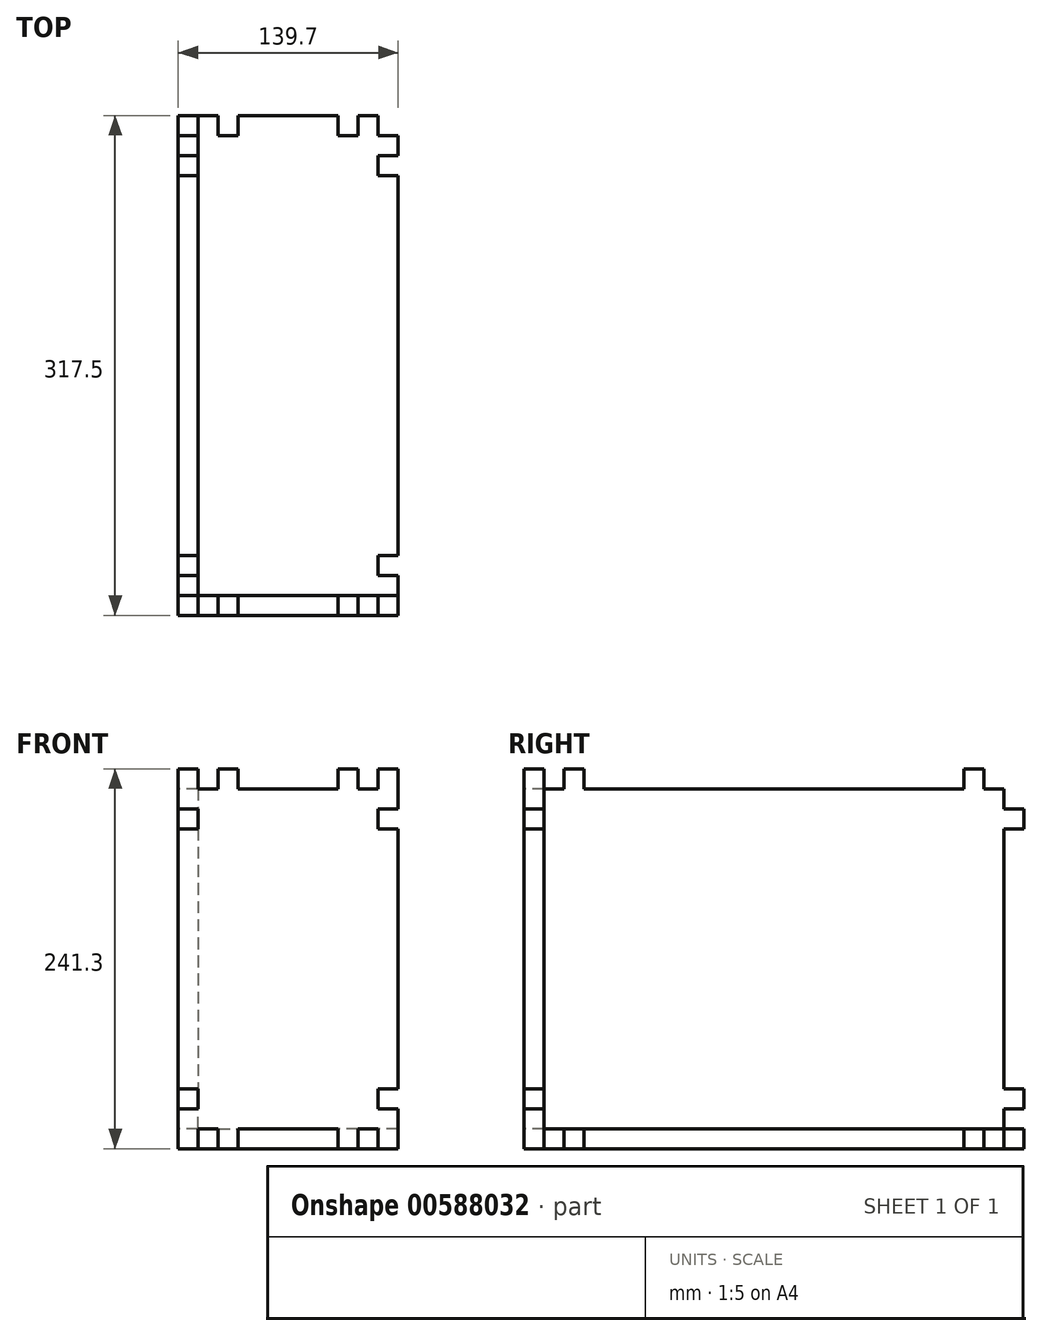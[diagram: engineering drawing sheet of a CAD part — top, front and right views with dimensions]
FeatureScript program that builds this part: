
annotation { "Feature Type Name" : "Feature", "Feature Type Description" : "" }
export const myFeature = defineFeature(function(context is Context, id is Id, definition is map)
    precondition{}
    {
        {
            var Q0;
            Q0=qCreatedBy(makeId("Top.planeOp"),FACE);
            var sketch = newSketch(context, id + "F0", { "sketchPlane" : qUnion([Q0])});
            skLineSegment(sketch, "E0.bottom", {"start": v(0, 0) * mm, "end": v(139.7, 0) * mm});
            skLineSegment(sketch, "E0.top", {"start": v(0, 317.5) * mm, "end": v(139.7, 317.5) * mm});
            skLineSegment(sketch, "E0.left", {"start": v(0, 0) * mm, "end": v(0, 317.5) * mm});
            skLineSegment(sketch, "E0.right", {"start": v(139.7, 0) * mm, "end": v(139.7, 317.5) * mm});
            skLineSegment(sketch, "E1", {"start": v(0, 0) * mm, "end": v(0, 12.7) * mm});
            skLineSegment(sketch, "E2", {"start": v(0, 12.7) * mm, "end": v(12.7, 12.7) * mm});
            skLineSegment(sketch, "E3", {"start": v(12.7, 12.7) * mm, "end": v(12.7, 0) * mm});
            skLineSegment(sketch, "E4", {"start": v(12.7, 0) * mm, "end": v(25.4, 0) * mm});
            skLineSegment(sketch, "E5", {"start": v(25.4, 0) * mm, "end": v(25.4, 12.7) * mm});
            skLineSegment(sketch, "E6", {"start": v(25.4, 12.7) * mm, "end": v(38.1, 12.7) * mm});
            skLineSegment(sketch, "E7", {"start": v(38.1, 12.7) * mm, "end": v(38.1, 0) * mm});
            skLineSegment(sketch, "E8", {"start": v(0, 12.7) * mm, "end": v(0, 25.4) * mm});
            skLineSegment(sketch, "E9", {"start": v(0, 25.4) * mm, "end": v(12.7, 25.4) * mm});
            skLineSegment(sketch, "E10", {"start": v(12.7, 25.4) * mm, "end": v(12.7, 38.1) * mm});
            skLineSegment(sketch, "E11", {"start": v(12.7, 38.1) * mm, "end": v(0, 38.1) * mm});
            skLineSegment(sketch, "E12", {"start": v(0, 158.75) * mm, "end": v(30.82, 158.75) * mm});
            skLineSegment(sketch, "E13", {"start": v(69.85, 0) * mm, "end": v(69.85, 38.66) * mm});
            skLineSegment(sketch, "E14.MirrorCS", {"start": v(0, 292.1) * mm, "end": v(12.7, 292.1) * mm});
            skLineSegment(sketch, "E15.MirrorCS", {"start": v(0, 304.8) * mm, "end": v(0, 292.1) * mm});
            skLineSegment(sketch, "E16.MirrorCS", {"start": v(12.7, 292.1) * mm, "end": v(12.7, 279.4) * mm});
            skLineSegment(sketch, "E17.MirrorCS", {"start": v(12.7, 279.4) * mm, "end": v(0, 279.4) * mm});
            skLineSegment(sketch, "E18.MirrorCS", {"start": v(0, 317.5) * mm, "end": v(0, 304.8) * mm});
            skLineSegment(sketch, "E19.MirrorCS", {"start": v(38.1, 304.8) * mm, "end": v(38.1, 317.5) * mm});
            skLineSegment(sketch, "E20.MirrorCS", {"start": v(25.4, 304.8) * mm, "end": v(38.1, 304.8) * mm});
            skLineSegment(sketch, "E21.MirrorCS", {"start": v(25.4, 317.5) * mm, "end": v(25.4, 304.8) * mm});
            skLineSegment(sketch, "E22.MirrorCS", {"start": v(12.7, 317.5) * mm, "end": v(25.4, 317.5) * mm});
            skLineSegment(sketch, "E23.MirrorCS", {"start": v(0, 304.8) * mm, "end": v(12.7, 304.8) * mm});
            skLineSegment(sketch, "E24.MirrorCS", {"start": v(12.7, 304.8) * mm, "end": v(12.7, 317.5) * mm});
            skLineSegment(sketch, "E25.MirrorCS", {"start": v(0, 317.5) * mm, "end": v(0, 0) * mm});
            skLineSegment(sketch, "E26.MirrorCS", {"start": v(101.6, 304.8) * mm, "end": v(101.6, 317.5) * mm});
            skLineSegment(sketch, "E27.MirrorCS", {"start": v(114.3, 304.8) * mm, "end": v(101.6, 304.8) * mm});
            skLineSegment(sketch, "E28.MirrorCS", {"start": v(127, 317.5) * mm, "end": v(114.3, 317.5) * mm});
            skLineSegment(sketch, "E29.MirrorCS", {"start": v(114.3, 317.5) * mm, "end": v(114.3, 304.8) * mm});
            skLineSegment(sketch, "E30.MirrorCS", {"start": v(127, 304.8) * mm, "end": v(127, 317.5) * mm});
            skLineSegment(sketch, "E31.MirrorCS", {"start": v(139.7, 304.8) * mm, "end": v(127, 304.8) * mm});
            skLineSegment(sketch, "E32.MirrorCS", {"start": v(139.7, 304.8) * mm, "end": v(139.7, 292.1) * mm});
            skLineSegment(sketch, "E33.MirrorCS", {"start": v(139.7, 292.1) * mm, "end": v(127, 292.1) * mm});
            skLineSegment(sketch, "E34.MirrorCS", {"start": v(127, 292.1) * mm, "end": v(127, 279.4) * mm});
            skLineSegment(sketch, "E35.MirrorCS", {"start": v(127, 279.4) * mm, "end": v(139.7, 279.4) * mm});
            skLineSegment(sketch, "E36.MirrorCS", {"start": v(127, 38.1) * mm, "end": v(139.7, 38.1) * mm});
            skLineSegment(sketch, "E37.MirrorCS", {"start": v(101.6, 12.7) * mm, "end": v(101.6, 0) * mm});
            skLineSegment(sketch, "E38.MirrorCS", {"start": v(114.3, 12.7) * mm, "end": v(101.6, 12.7) * mm});
            skLineSegment(sketch, "E39.MirrorCS", {"start": v(127, 0) * mm, "end": v(114.3, 0) * mm});
            skLineSegment(sketch, "E40.MirrorCS", {"start": v(114.3, 0) * mm, "end": v(114.3, 12.7) * mm});
            skLineSegment(sketch, "E41.MirrorCS", {"start": v(127, 12.7) * mm, "end": v(127, 0) * mm});
            skLineSegment(sketch, "E42.MirrorCS", {"start": v(139.7, 12.7) * mm, "end": v(127, 12.7) * mm});
            skLineSegment(sketch, "E43.MirrorCS", {"start": v(139.7, 12.7) * mm, "end": v(139.7, 25.4) * mm});
            skLineSegment(sketch, "E44.MirrorCS", {"start": v(127, 25.4) * mm, "end": v(127, 38.1) * mm});
            skLineSegment(sketch, "E45.MirrorCS", {"start": v(139.7, 25.4) * mm, "end": v(127, 25.4) * mm});
            skSolve(sketch);
        }
        {
            var Q0;
            Q0=makeQuery(id+"F0.imprint","IMPRINT",FACE,{"disambiguationData":[TD([[makeQuery(id+"F0.imprint","IMPRINT",EDGE,{"derivedFrom":sQuery(id+"F0.wireOp",EDGE,"E16.MirrorCS")}),1.0]])]});
            extrude(context, id + "F1", {"entities" : qUnion([Q0]), "oppositeDirection" : true, "depth" : 12.7 * mm, "offsetDistance" : 25.4 * mm});
        }
        {
            var Q0;
            Q0=qCreatedBy(makeId("Front.planeOp"),FACE);
            var sketch = newSketch(context, id + "F2", { "sketchPlane" : qUnion([Q0])});
            skLineSegment(sketch, "E46", {"start": v(0, 0) * mm, "end": v(0, -12.7) * mm});
            skLineSegment(sketch, "E47", {"start": v(0, -12.7) * mm, "end": v(12.7, -12.7) * mm});
            skLineSegment(sketch, "E48", {"start": v(12.7, -12.7) * mm, "end": v(12.7, 0) * mm});
            skLineSegment(sketch, "E49", {"start": v(12.7, 0) * mm, "end": v(25.4, 0) * mm});
            skLineSegment(sketch, "E50", {"start": v(25.4, 0) * mm, "end": v(25.4, -12.7) * mm});
            skLineSegment(sketch, "E51", {"start": v(25.4, -12.7) * mm, "end": v(38.1, -12.7) * mm});
            skLineSegment(sketch, "E52", {"start": v(0, 0) * mm, "end": v(0, 12.7) * mm});
            skLineSegment(sketch, "E53", {"start": v(0, 12.7) * mm, "end": v(12.7, 12.7) * mm});
            skLineSegment(sketch, "E54", {"start": v(12.7, 12.7) * mm, "end": v(12.7, 25.4) * mm});
            skLineSegment(sketch, "E55", {"start": v(12.7, 25.4) * mm, "end": v(0, 25.4) * mm});
            skLineSegment(sketch, "E56.bottom", {"start": v(0, -12.7) * mm, "end": v(139.7, -12.7) * mm});
            skLineSegment(sketch, "E56.top", {"start": v(0, 228.6) * mm, "end": v(139.7, 228.6) * mm});
            skLineSegment(sketch, "E56.left", {"start": v(0, -12.7) * mm, "end": v(0, 228.6) * mm});
            skLineSegment(sketch, "E56.right", {"start": v(139.7, -12.7) * mm, "end": v(139.7, 228.6) * mm});
            skLineSegment(sketch, "E57", {"start": v(69.85, -12.7) * mm, "end": v(69.85, 21.02) * mm});
            skLineSegment(sketch, "E58", {"start": v(0, 107.95) * mm, "end": v(42.02, 107.95) * mm});
            skLineSegment(sketch, "E59.MirrorCS", {"start": v(127, -12.7) * mm, "end": v(127, 0) * mm});
            skLineSegment(sketch, "E60.MirrorCS", {"start": v(114.3, -12.7) * mm, "end": v(101.6, -12.7) * mm});
            skLineSegment(sketch, "E61.MirrorCS", {"start": v(127, 0) * mm, "end": v(114.3, 0) * mm});
            skLineSegment(sketch, "E62.MirrorCS", {"start": v(139.7, 0) * mm, "end": v(139.7, 12.7) * mm});
            skLineSegment(sketch, "E63.MirrorCS", {"start": v(127, 12.7) * mm, "end": v(127, 25.4) * mm});
            skLineSegment(sketch, "E64.MirrorCS", {"start": v(139.7, 12.7) * mm, "end": v(127, 12.7) * mm});
            skLineSegment(sketch, "E65.MirrorCS", {"start": v(139.7, -12.7) * mm, "end": v(127, -12.7) * mm});
            skLineSegment(sketch, "E66.MirrorCS", {"start": v(139.7, 0) * mm, "end": v(139.7, -12.7) * mm});
            skLineSegment(sketch, "E67.MirrorCS", {"start": v(114.3, 0) * mm, "end": v(114.3, -12.7) * mm});
            skLineSegment(sketch, "E68.MirrorCS", {"start": v(127, 25.4) * mm, "end": v(139.7, 25.4) * mm});
            skLineSegment(sketch, "E69.MirrorCS", {"start": v(12.7, 190.5) * mm, "end": v(0, 190.5) * mm});
            skLineSegment(sketch, "E70.MirrorCS", {"start": v(12.7, 203.2) * mm, "end": v(12.7, 190.5) * mm});
            skLineSegment(sketch, "E71.MirrorCS", {"start": v(0, 203.2) * mm, "end": v(12.7, 203.2) * mm});
            skLineSegment(sketch, "E72.MirrorCS", {"start": v(0, 228.6) * mm, "end": v(12.7, 228.6) * mm});
            skLineSegment(sketch, "E73.MirrorCS", {"start": v(25.4, 215.9) * mm, "end": v(25.4, 228.6) * mm});
            skLineSegment(sketch, "E74.MirrorCS", {"start": v(12.7, 228.6) * mm, "end": v(12.7, 215.9) * mm});
            skLineSegment(sketch, "E75.MirrorCS", {"start": v(0, 215.9) * mm, "end": v(0, 228.6) * mm});
            skLineSegment(sketch, "E76.MirrorCS", {"start": v(12.7, 215.9) * mm, "end": v(25.4, 215.9) * mm});
            skLineSegment(sketch, "E77.MirrorCS", {"start": v(0, 215.9) * mm, "end": v(0, 203.2) * mm});
            skLineSegment(sketch, "E78.MirrorCS", {"start": v(25.4, 228.6) * mm, "end": v(38.1, 228.6) * mm});
            skLineSegment(sketch, "E79.MirrorCS", {"start": v(139.7, 215.9) * mm, "end": v(139.7, 228.6) * mm});
            skLineSegment(sketch, "E80.MirrorCS", {"start": v(114.3, 228.6) * mm, "end": v(101.6, 228.6) * mm});
            skLineSegment(sketch, "E81.MirrorCS", {"start": v(127, 215.9) * mm, "end": v(114.3, 215.9) * mm});
            skLineSegment(sketch, "E82.MirrorCS", {"start": v(139.7, 228.6) * mm, "end": v(127, 228.6) * mm});
            skLineSegment(sketch, "E83.MirrorCS", {"start": v(127, 228.6) * mm, "end": v(127, 215.9) * mm});
            skLineSegment(sketch, "E84.MirrorCS", {"start": v(139.7, 215.9) * mm, "end": v(139.7, 203.2) * mm});
            skLineSegment(sketch, "E85.MirrorCS", {"start": v(127, 203.2) * mm, "end": v(127, 190.5) * mm});
            skLineSegment(sketch, "E86.MirrorCS", {"start": v(139.7, 228.6) * mm, "end": v(139.7, -12.7) * mm});
            skLineSegment(sketch, "E87.MirrorCS", {"start": v(114.3, 215.9) * mm, "end": v(114.3, 228.6) * mm});
            skLineSegment(sketch, "E88.MirrorCS", {"start": v(127, 190.5) * mm, "end": v(139.7, 190.5) * mm});
            skLineSegment(sketch, "E89.MirrorCS", {"start": v(139.7, 203.2) * mm, "end": v(127, 203.2) * mm});
            skLineSegment(sketch, "E90", {"start": v(38.1, -12.7) * mm, "end": v(38.1, 0) * mm});
            skLineSegment(sketch, "E91", {"start": v(101.6, -12.7) * mm, "end": v(101.6, 0) * mm});
            skLineSegment(sketch, "E92", {"start": v(101.6, 0) * mm, "end": v(38.1, 0) * mm});
            skLineSegment(sketch, "E93", {"start": v(38.1, 228.6) * mm, "end": v(38.1, 215.9) * mm});
            skLineSegment(sketch, "E94", {"start": v(38.1, 215.9) * mm, "end": v(101.6, 215.9) * mm});
            skLineSegment(sketch, "E95", {"start": v(101.6, 215.9) * mm, "end": v(101.6, 228.6) * mm});
            skSolve(sketch);
        }
        {
            var Q0;
            {var subQ10=sQuery(id+"F2.wireOp",EDGE,"E48");Q0=makeQuery(id+"F2.imprint","IMPRINT",FACE,{"disambiguationData":[TD([[makeQuery(id+"F2.imprint","IMPRINT",EDGE,{"derivedFrom":subQ10}),1.0]])]});}
            extrude(context, id + "F3", {"entities" : qUnion([Q0]), "oppositeDirection" : true, "depth" : 12.7 * mm, "offsetDistance" : 25.4 * mm});
        }
        {
            var Q0;
            Q0=qCreatedBy(makeId("Right.planeOp"),FACE);
            var sketch = newSketch(context, id + "F4", { "sketchPlane" : qUnion([Q0])});
            skLineSegment(sketch, "E96", {"start": v(0, 0) * mm, "end": v(12.7, 0) * mm});
            skLineSegment(sketch, "E97", {"start": v(12.7, 0) * mm, "end": v(12.7, 12.7) * mm});
            skLineSegment(sketch, "E98", {"start": v(12.7, 12.7) * mm, "end": v(0, 12.7) * mm});
            skLineSegment(sketch, "E99", {"start": v(0, 12.7) * mm, "end": v(0, 25.4) * mm});
            skLineSegment(sketch, "E100", {"start": v(0, 25.4) * mm, "end": v(12.7, 25.4) * mm});
            skLineSegment(sketch, "E101", {"start": v(12.7, 0) * mm, "end": v(25.4, 0) * mm});
            skLineSegment(sketch, "E102", {"start": v(25.4, 0) * mm, "end": v(25.4, -12.7) * mm});
            skLineSegment(sketch, "E103", {"start": v(25.4, -12.7) * mm, "end": v(38.1, -12.7) * mm});
            skLineSegment(sketch, "E104", {"start": v(38.1, -12.7) * mm, "end": v(38.1, 0) * mm});
            skLineSegment(sketch, "E105", {"start": v(0, 0) * mm, "end": v(0, -12.7) * mm});
            skLineSegment(sketch, "E106.bottom", {"start": v(0, -12.7) * mm, "end": v(317.5, -12.7) * mm});
            skLineSegment(sketch, "E106.top", {"start": v(0, 228.6) * mm, "end": v(317.5, 228.6) * mm});
            skLineSegment(sketch, "E106.left", {"start": v(0, -12.7) * mm, "end": v(0, 228.6) * mm});
            skLineSegment(sketch, "E106.right", {"start": v(317.5, -12.7) * mm, "end": v(317.5, 228.6) * mm});
            skLineSegment(sketch, "E107", {"start": v(158.75, 228.6) * mm, "end": v(158.75, 170.9) * mm});
            skLineSegment(sketch, "E108", {"start": v(0, 107.95) * mm, "end": v(67.23, 107.95) * mm});
            skLineSegment(sketch, "E109.MirrorCS", {"start": v(12.7, 215.9) * mm, "end": v(12.7, 203.2) * mm});
            skLineSegment(sketch, "E110.MirrorCS", {"start": v(0, 215.9) * mm, "end": v(12.7, 215.9) * mm});
            skLineSegment(sketch, "E111.MirrorCS", {"start": v(25.4, 215.9) * mm, "end": v(25.4, 228.6) * mm});
            skLineSegment(sketch, "E112.MirrorCS", {"start": v(38.1, 228.6) * mm, "end": v(38.1, 215.9) * mm});
            skLineSegment(sketch, "E113.MirrorCS", {"start": v(0, 215.9) * mm, "end": v(0, 228.6) * mm});
            skLineSegment(sketch, "E114.MirrorCS", {"start": v(25.4, 228.6) * mm, "end": v(38.1, 228.6) * mm});
            skLineSegment(sketch, "E115.MirrorCS", {"start": v(12.7, 215.9) * mm, "end": v(25.4, 215.9) * mm});
            skLineSegment(sketch, "E116.MirrorCS", {"start": v(0, 190.5) * mm, "end": v(12.7, 190.5) * mm});
            skLineSegment(sketch, "E117.MirrorCS", {"start": v(0, 203.2) * mm, "end": v(0, 190.5) * mm});
            skLineSegment(sketch, "E118.MirrorCS", {"start": v(12.7, 203.2) * mm, "end": v(0, 203.2) * mm});
            skLineSegment(sketch, "E119.MirrorCS", {"start": v(292.1, 0) * mm, "end": v(292.1, -12.7) * mm});
            skLineSegment(sketch, "E120.MirrorCS", {"start": v(304.8, 12.7) * mm, "end": v(317.5, 12.7) * mm});
            skLineSegment(sketch, "E121.MirrorCS", {"start": v(317.5, 12.7) * mm, "end": v(317.5, 25.4) * mm});
            skLineSegment(sketch, "E122.MirrorCS", {"start": v(317.5, 0) * mm, "end": v(304.8, 0) * mm});
            skLineSegment(sketch, "E123.MirrorCS", {"start": v(317.5, 0) * mm, "end": v(317.5, -12.7) * mm});
            skLineSegment(sketch, "E124.MirrorCS", {"start": v(292.1, -12.7) * mm, "end": v(279.4, -12.7) * mm});
            skLineSegment(sketch, "E125.MirrorCS", {"start": v(304.8, 0) * mm, "end": v(292.1, 0) * mm});
            skLineSegment(sketch, "E126.MirrorCS", {"start": v(304.8, 0) * mm, "end": v(304.8, 12.7) * mm});
            skLineSegment(sketch, "E127.MirrorCS", {"start": v(279.4, -12.7) * mm, "end": v(279.4, 0) * mm});
            skLineSegment(sketch, "E128.MirrorCS", {"start": v(317.5, 25.4) * mm, "end": v(304.8, 25.4) * mm});
            skLineSegment(sketch, "E129.MirrorCS", {"start": v(317.5, -12.7) * mm, "end": v(0, -12.7) * mm});
            skLineSegment(sketch, "E130.MirrorCS", {"start": v(317.5, 215.9) * mm, "end": v(304.8, 215.9) * mm});
            skLineSegment(sketch, "E131.MirrorCS", {"start": v(292.1, 228.6) * mm, "end": v(279.4, 228.6) * mm});
            skLineSegment(sketch, "E132.MirrorCS", {"start": v(317.5, 203.2) * mm, "end": v(317.5, 190.5) * mm});
            skLineSegment(sketch, "E133.MirrorCS", {"start": v(292.1, 215.9) * mm, "end": v(292.1, 228.6) * mm});
            skLineSegment(sketch, "E134.MirrorCS", {"start": v(317.5, 215.9) * mm, "end": v(317.5, 228.6) * mm});
            skLineSegment(sketch, "E135.MirrorCS", {"start": v(304.8, 215.9) * mm, "end": v(304.8, 203.2) * mm});
            skLineSegment(sketch, "E136.MirrorCS", {"start": v(304.8, 203.2) * mm, "end": v(317.5, 203.2) * mm});
            skLineSegment(sketch, "E137.MirrorCS", {"start": v(304.8, 215.9) * mm, "end": v(292.1, 215.9) * mm});
            skLineSegment(sketch, "E138.MirrorCS", {"start": v(317.5, 190.5) * mm, "end": v(304.8, 190.5) * mm});
            skLineSegment(sketch, "E139.MirrorCS", {"start": v(279.4, 228.6) * mm, "end": v(279.4, 215.9) * mm});
            skLineSegment(sketch, "E140", {"start": v(12.7, 190.5) * mm, "end": v(12.7, 25.4) * mm});
            skLineSegment(sketch, "E141", {"start": v(38.1, 0) * mm, "end": v(279.4, 0) * mm});
            skLineSegment(sketch, "E142", {"start": v(304.8, 25.4) * mm, "end": v(304.8, 190.5) * mm});
            skLineSegment(sketch, "E143", {"start": v(279.4, 215.9) * mm, "end": v(38.1, 215.9) * mm});
            skSolve(sketch);
        }
        {
            var Q0;
            Q0=makeQuery(id+"F4.imprint","IMPRINT",FACE,{"disambiguationData":[TD([[makeQuery(id+"F4.imprint","IMPRINT",EDGE,{"derivedFrom":sQuery(id+"F4.wireOp",EDGE,"E97")}),-1.0]])]});
            extrude(context, id + "F5", {"entities" : qUnion([Q0]), "depth" : 12.7 * mm, "offsetDistance" : 25.4 * mm});
        }
    });
